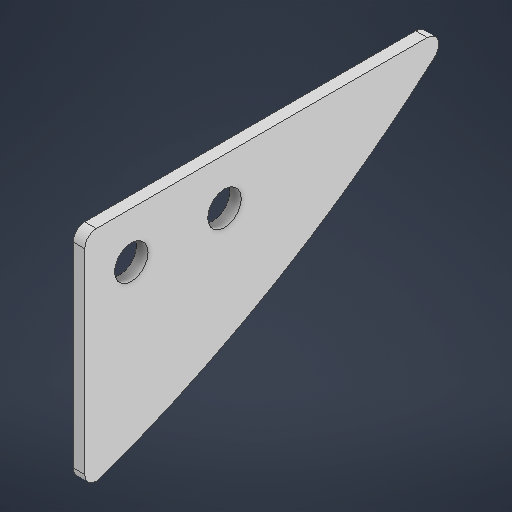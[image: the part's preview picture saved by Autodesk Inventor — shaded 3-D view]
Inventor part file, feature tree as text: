
AUTODESK INVENTOR PART (.ipt)
format: ipt  version: 2025.2 (Build 292293000, 293)  size: 187,904 bytes
history: native  units: in
note: dims shown in document units (in); Inventor stores cm internally (conversion verified against a paired STEP export)
features: extrude x1, sketch x1
ambient origin geometry x8: Origin, YZ Plane, XZ Plane, XY Plane, X Axis, Y Axis, Z Axis, Center Point
bodies: Solid1 (feature_tree)
feature tree (2):
  extrude  "Extrusion1"  Depth=0.0625in
  sketch  "Sketch1"  dims[d0=1.2in d1=1.5in d6=0.18in d7=0.18in d10=2.0in d13=0.0625in d14=0.0625in d15=0.0in d16=0.0625in]
